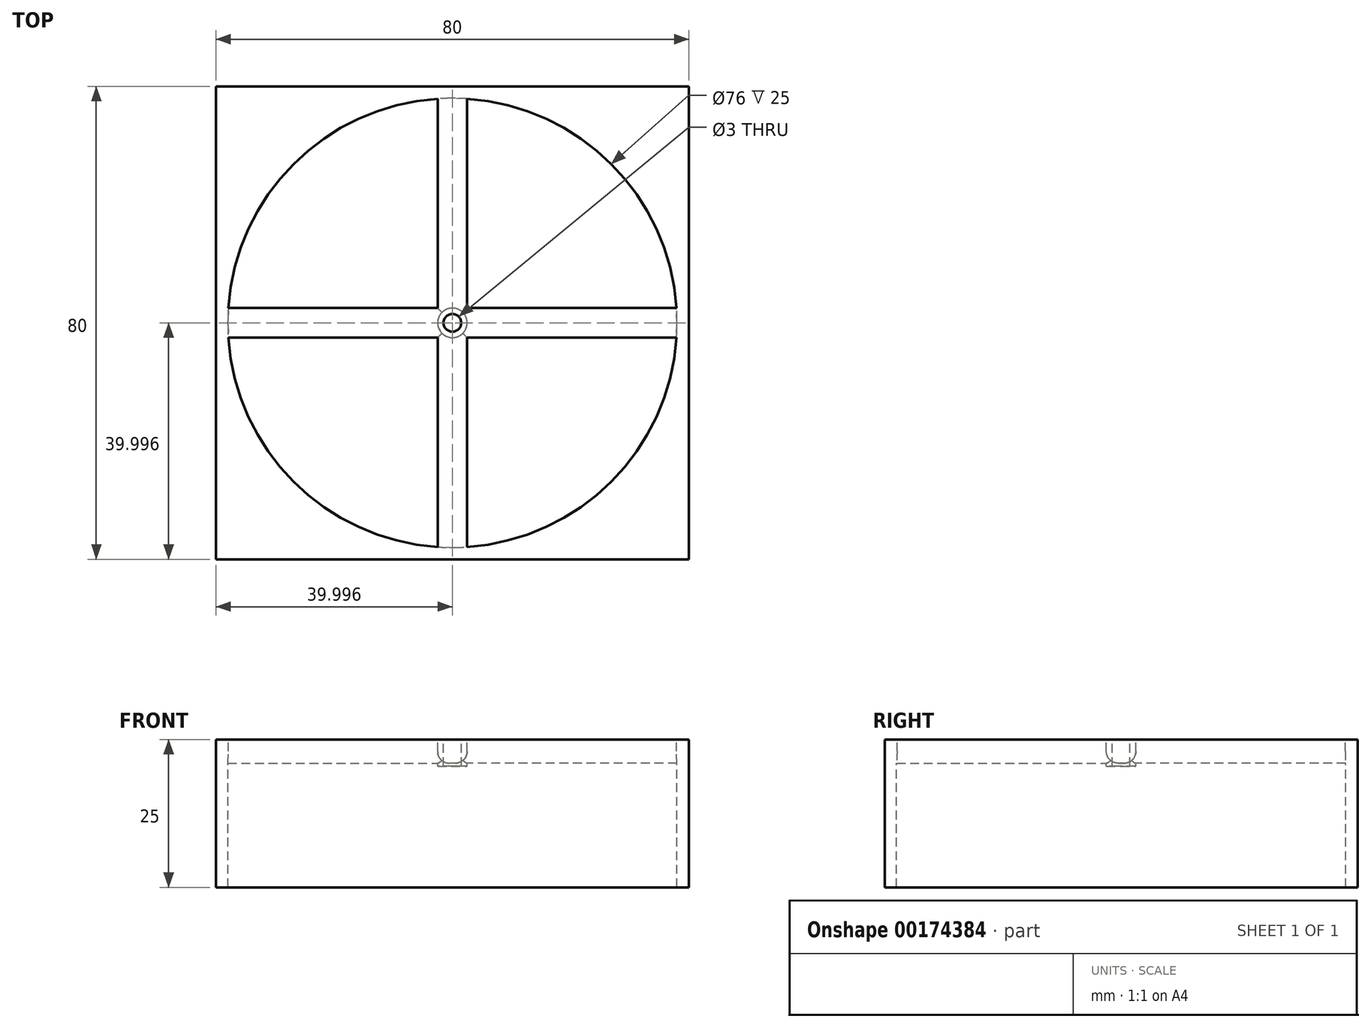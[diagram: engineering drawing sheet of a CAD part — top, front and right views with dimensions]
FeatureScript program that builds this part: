
annotation { "Feature Type Name" : "Feature", "Feature Type Description" : "" }
export const myFeature = defineFeature(function(context is Context, id is Id, definition is map)
    precondition{}
    {
        {
            var Q0;
            Q0=qCreatedBy(makeId("Top.planeOp"),FACE);
            var sketch = newSketch(context, id + "F0", { "sketchPlane" : qUnion([Q0])});
            skLineSegment(sketch, "E0.bottom", {"start": v(-45.8, 42.93) * mm, "end": v(34.2, 42.93) * mm});
            skLineSegment(sketch, "E0.top", {"start": v(-45.8, -37.07) * mm, "end": v(34.2, -37.07) * mm});
            skLineSegment(sketch, "E0.left", {"start": v(-45.8, 42.93) * mm, "end": v(-45.8, -37.07) * mm});
            skLineSegment(sketch, "E0.right", {"start": v(34.2, 42.93) * mm, "end": v(34.2, -37.07) * mm});
            skSolve(sketch);
        }
        {
            var Q0;
            Q0 = qSketchRegion(id + "F0", true);
            extrude(context, id + "F1", {"entities" : qUnion([Q0]), "depth" : 25 * mm});
        }
        {
            var Q0;
            Q0=makeQuery(id+"F1.opExtrude","CAP_FACE",FACE,{"disambiguationData":[OSD([sQuery(id+"F0.wireOp",EDGE,"E0.bottom"),sQuery(id+"F0.wireOp",EDGE,"E0.top"),sQuery(id+"F0.wireOp",EDGE,"E0.left"),sQuery(id+"F0.wireOp",EDGE,"E0.right")])],"isStart":false});
            var sketch = newSketch(context, id + "F2", { "sketchPlane" : qUnion([Q0])});
            skLineSegment(sketch, "E1", {"start": v(-45.8, 42.93) * mm, "end": v(34.2, -37.07) * mm});
            skLineSegment(sketch, "E2", {"start": v(-45.8, -37.07) * mm, "end": v(34.2, 42.93) * mm});
            skCircle(sketch, "E3", {"center": v(-5.8, 2.93) * mm, "radius": 38 * mm});
            skSolve(sketch);
        }
        {
            var Q0;
            Q0 = qSketchRegion(id + "F2", true);
            extrude(context, id + "F3", {"entities" : qUnion([Q0]), "operationType" : NewBodyOperationType.REMOVE, "oppositeDirection" : true, "depth" : 25 * mm});
        }
        {
            var Q0;
            Q0=makeQuery(id+"F1.opExtrude","CAP_FACE",FACE,{"disambiguationData":[OSD([sQuery(id+"F0.wireOp",EDGE,"E0.bottom"),sQuery(id+"F0.wireOp",EDGE,"E0.top"),sQuery(id+"F0.wireOp",EDGE,"E0.left"),sQuery(id+"F0.wireOp",EDGE,"E0.right")])],"isStart":false});
            var sketch = newSketch(context, id + "F4", { "sketchPlane" : qUnion([Q0])});
            skLineSegment(sketch, "E4", {"start": v(-5.8, -37.07) * mm, "end": v(-8.3, -37.07) * mm});
            skLineSegment(sketch, "E5", {"start": v(-8.3, -37.07) * mm, "end": v(-8.3, 42.93) * mm});
            skLineSegment(sketch, "E6", {"start": v(-8.3, 42.93) * mm, "end": v(-3.3, 42.93) * mm});
            skLineSegment(sketch, "E7", {"start": v(-3.3, 42.93) * mm, "end": v(-3.3, -37.07) * mm});
            skLineSegment(sketch, "E8", {"start": v(-3.3, -37.07) * mm, "end": v(-5.8, -37.07) * mm});
            skLineSegment(sketch, "E9.MirrorCS", {"start": v(-45.8, 0.43) * mm, "end": v(34.2, 0.43) * mm});
            skLineSegment(sketch, "E10.MirrorCS", {"start": v(-45.8, 5.43) * mm, "end": v(-45.8, 0.43) * mm});
            skLineSegment(sketch, "E11.MirrorCS", {"start": v(34.2, 5.43) * mm, "end": v(-45.8, 5.43) * mm});
            skLineSegment(sketch, "E12", {"start": v(34.2, 0.43) * mm, "end": v(34.2, 5.43) * mm});
            skLineSegment(sketch, "E13", {"start": v(-3.3, 0.43) * mm, "end": v(-8.3, 5.43) * mm});
            skLineSegment(sketch, "E14", {"start": v(-8.3, 0.43) * mm, "end": v(-3.3, 5.43) * mm});
            skCircle(sketch, "E15", {"center": v(-5.8, 2.93) * mm, "radius": 1.5 * mm});
            skSolve(sketch);
        }
        {
            var Q0;
            Q0 = qSketchRegion(id + "F4", true);
            extrude(context, id + "F5", {"entities" : qUnion([Q0]), "operationType" : NewBodyOperationType.ADD, "oppositeDirection" : true, "depth" : 4 * mm});
        }
        {
            var Q0;
            {var subQ0=sQuery(id+"F4.wireOp",EDGE,"E7");var subQ1=makeQuery(id+"F4.imprint","INTERSECT",VERTEX,{"disambiguationData":[OD(0.0)],"derivedFrom":[makeQuery(id+"F3.boolean.opBoolean","COPY",EDGE,{"derivedFrom":makeQuery(id+"F3.opExtrude","CAP_EDGE",EDGE,{"disambiguationData":[OSD([sQuery(id+"F2.wireOp",EDGE,"E3")])],"isStart":true})}),subQ0]});Q0=makeQuery(id+"F5.opExtrude","CAP_EDGE",EDGE,{"disambiguationData":[OSD([subQ0]),TDD([makeQuery(id+"F4.imprint","IMPRINT",EDGE,{"disambiguationData":[TD([[subQ1,1.0]])],"derivedFrom":subQ0}),makeQuery(id+"F4.imprint","IMPRINT",EDGE,{"disambiguationData":[TD([[subQ1,-1.0]])],"derivedFrom":subQ0})])],"isStart":false});}
            var Q1;
            {var subQ0=sQuery(id+"F4.wireOp",EDGE,"E5");var subQ1=makeQuery(id+"F4.imprint","INTERSECT",VERTEX,{"disambiguationData":[OD(1.0)],"derivedFrom":[makeQuery(id+"F3.boolean.opBoolean","COPY",EDGE,{"derivedFrom":makeQuery(id+"F3.opExtrude","CAP_EDGE",EDGE,{"disambiguationData":[OSD([sQuery(id+"F2.wireOp",EDGE,"E3")])],"isStart":true})}),subQ0]});Q1=makeQuery(id+"F5.opExtrude","CAP_EDGE",EDGE,{"disambiguationData":[OSD([subQ0]),TDD([makeQuery(id+"F4.imprint","IMPRINT",EDGE,{"disambiguationData":[TD([[subQ1,1.0]])],"derivedFrom":subQ0}),makeQuery(id+"F4.imprint","IMPRINT",EDGE,{"disambiguationData":[TD([[subQ1,-1.0]])],"derivedFrom":subQ0})])],"isStart":false});}
            var Q2;
            {var subQ0=sQuery(id+"F4.wireOp",EDGE,"E9.MirrorCS");var subQ1=makeQuery(id+"F4.imprint","INTERSECT",VERTEX,{"disambiguationData":[OD(0.0)],"derivedFrom":[makeQuery(id+"F3.boolean.opBoolean","COPY",EDGE,{"derivedFrom":makeQuery(id+"F3.opExtrude","CAP_EDGE",EDGE,{"disambiguationData":[OSD([sQuery(id+"F2.wireOp",EDGE,"E3")])],"isStart":true})}),subQ0]});Q2=makeQuery(id+"F5.opExtrude","CAP_EDGE",EDGE,{"disambiguationData":[OSD([subQ0]),TDD([makeQuery(id+"F4.imprint","IMPRINT",EDGE,{"disambiguationData":[TD([[subQ1,1.0]])],"derivedFrom":subQ0}),makeQuery(id+"F4.imprint","IMPRINT",EDGE,{"disambiguationData":[TD([[subQ1,-1.0]])],"derivedFrom":subQ0})])],"isStart":false});}
            var Q3;
            {var subQ0=sQuery(id+"F4.wireOp",EDGE,"E11.MirrorCS");var subQ1=makeQuery(id+"F4.imprint","INTERSECT",VERTEX,{"disambiguationData":[OD(0.0)],"derivedFrom":[makeQuery(id+"F3.boolean.opBoolean","COPY",EDGE,{"derivedFrom":makeQuery(id+"F3.opExtrude","CAP_EDGE",EDGE,{"disambiguationData":[OSD([sQuery(id+"F2.wireOp",EDGE,"E3")])],"isStart":true})}),subQ0]});Q3=makeQuery(id+"F5.opExtrude","CAP_EDGE",EDGE,{"disambiguationData":[OSD([subQ0]),TDD([makeQuery(id+"F4.imprint","IMPRINT",EDGE,{"disambiguationData":[TD([[subQ1,1.0]])],"derivedFrom":subQ0}),makeQuery(id+"F4.imprint","IMPRINT",EDGE,{"disambiguationData":[TD([[subQ1,-1.0]])],"derivedFrom":subQ0})])],"isStart":false});}
            var Q4;
            {var subQ0=sQuery(id+"F4.wireOp",EDGE,"E9.MirrorCS");var subQ1=makeQuery(id+"F4.imprint","INTERSECT",VERTEX,{"disambiguationData":[OD(1.0)],"derivedFrom":[makeQuery(id+"F3.boolean.opBoolean","COPY",EDGE,{"derivedFrom":makeQuery(id+"F3.opExtrude","CAP_EDGE",EDGE,{"disambiguationData":[OSD([sQuery(id+"F2.wireOp",EDGE,"E3")])],"isStart":true})}),subQ0]});Q4=makeQuery(id+"F5.opExtrude","CAP_EDGE",EDGE,{"disambiguationData":[OSD([subQ0]),TDD([makeQuery(id+"F4.imprint","IMPRINT",EDGE,{"disambiguationData":[TD([[subQ1,1.0]])],"derivedFrom":subQ0}),makeQuery(id+"F4.imprint","IMPRINT",EDGE,{"disambiguationData":[TD([[subQ1,-1.0]])],"derivedFrom":subQ0})])],"isStart":false});}
            var Q5;
            {var subQ0=sQuery(id+"F4.wireOp",EDGE,"E11.MirrorCS");var subQ1=makeQuery(id+"F4.imprint","INTERSECT",VERTEX,{"disambiguationData":[OD(1.0)],"derivedFrom":[makeQuery(id+"F3.boolean.opBoolean","COPY",EDGE,{"derivedFrom":makeQuery(id+"F3.opExtrude","CAP_EDGE",EDGE,{"disambiguationData":[OSD([sQuery(id+"F2.wireOp",EDGE,"E3")])],"isStart":true})}),subQ0]});Q5=makeQuery(id+"F5.opExtrude","CAP_EDGE",EDGE,{"disambiguationData":[OSD([subQ0]),TDD([makeQuery(id+"F4.imprint","IMPRINT",EDGE,{"disambiguationData":[TD([[subQ1,1.0]])],"derivedFrom":subQ0}),makeQuery(id+"F4.imprint","IMPRINT",EDGE,{"disambiguationData":[TD([[subQ1,-1.0]])],"derivedFrom":subQ0})])],"isStart":false});}
            var Q6;
            {var subQ0=sQuery(id+"F4.wireOp",EDGE,"E7");var subQ1=makeQuery(id+"F4.imprint","INTERSECT",VERTEX,{"disambiguationData":[OD(1.0)],"derivedFrom":[makeQuery(id+"F3.boolean.opBoolean","COPY",EDGE,{"derivedFrom":makeQuery(id+"F3.opExtrude","CAP_EDGE",EDGE,{"disambiguationData":[OSD([sQuery(id+"F2.wireOp",EDGE,"E3")])],"isStart":true})}),subQ0]});Q6=makeQuery(id+"F5.opExtrude","CAP_EDGE",EDGE,{"disambiguationData":[OSD([subQ0]),TDD([makeQuery(id+"F4.imprint","IMPRINT",EDGE,{"disambiguationData":[TD([[subQ1,1.0]])],"derivedFrom":subQ0}),makeQuery(id+"F4.imprint","IMPRINT",EDGE,{"disambiguationData":[TD([[subQ1,-1.0]])],"derivedFrom":subQ0})])],"isStart":false});}
            var Q7;
            {var subQ0=sQuery(id+"F4.wireOp",EDGE,"E5");var subQ1=makeQuery(id+"F4.imprint","INTERSECT",VERTEX,{"disambiguationData":[OD(0.0)],"derivedFrom":[makeQuery(id+"F3.boolean.opBoolean","COPY",EDGE,{"derivedFrom":makeQuery(id+"F3.opExtrude","CAP_EDGE",EDGE,{"disambiguationData":[OSD([sQuery(id+"F2.wireOp",EDGE,"E3")])],"isStart":true})}),subQ0]});Q7=makeQuery(id+"F5.opExtrude","CAP_EDGE",EDGE,{"disambiguationData":[OSD([subQ0]),TDD([makeQuery(id+"F4.imprint","IMPRINT",EDGE,{"disambiguationData":[TD([[subQ1,1.0]])],"derivedFrom":subQ0}),makeQuery(id+"F4.imprint","IMPRINT",EDGE,{"disambiguationData":[TD([[subQ1,-1.0]])],"derivedFrom":subQ0})])],"isStart":false});}
            fillet(context, id + "F6", {"entities" : qUnion([Q0, Q1, Q2, Q3, Q4, Q5, Q6, Q7]), "radius" : 2 * mm, "tangentPropagation" : true, "allowEdgeOverflow" : false});
        }
        {
            var Q0;
            Q0=makeQuery(id+"F6.opFillet","SPLIT",FACE,{"disambiguationData":[OD(1.0)],"derivedFrom":makeQuery(id+"F5.opExtrude","CAP_FACE",FACE,{"disambiguationData":[OSD([sQuery(id+"F4.wireOp",EDGE,"E4"),sQuery(id+"F4.wireOp",EDGE,"E5"),sQuery(id+"F4.wireOp",EDGE,"E6"),sQuery(id+"F4.wireOp",EDGE,"E7"),sQuery(id+"F4.wireOp",EDGE,"E8"),sQuery(id+"F4.wireOp",EDGE,"E9.MirrorCS"),sQuery(id+"F4.wireOp",EDGE,"E10.MirrorCS"),sQuery(id+"F4.wireOp",EDGE,"E11.MirrorCS"),sQuery(id+"F4.wireOp",EDGE,"E12"),sQuery(id+"F4.wireOp",EDGE,"E15")])],"isStart":false})});
            var sketch = newSketch(context, id + "F7", { "sketchPlane" : qUnion([Q0])});
            skPoint(sketch, "E16.first.point", {"position": v(-5.8, -4.43) * mm});
            skPoint(sketch, "E16.second.point", {"position": v(-5.8, -1.35) * mm});
            skPoint(sketch, "E16.second.point.positionSnap0", {"position": v(-5.8, -4.43) * mm});
            skPoint(sketch, "E16.third.point", {"position": v(-7.27, -2.57) * mm});
            skLineSegment(sketch, "E17", {"start": v(-5.8, -4.43) * mm, "end": v(-5.8, -2.93) * mm});
            skCircle(sketch, "E18", {"center": v(-5.8, -2.93) * mm, "radius": 1.5 * mm});
            skCircle(sketch, "E19", {"center": v(-5.8, -2.93) * mm, "radius": 2.5 * mm});
            skSolve(sketch);
        }
        {
            var Q0;
            Q0 = qSketchRegion(id + "F7", true);
            extrude(context, id + "F8", {"entities" : qUnion([Q0]), "operationType" : NewBodyOperationType.ADD, "endBound" : BoundingType.SYMMETRIC, "depth" : 1 * mm});
        }
    });
